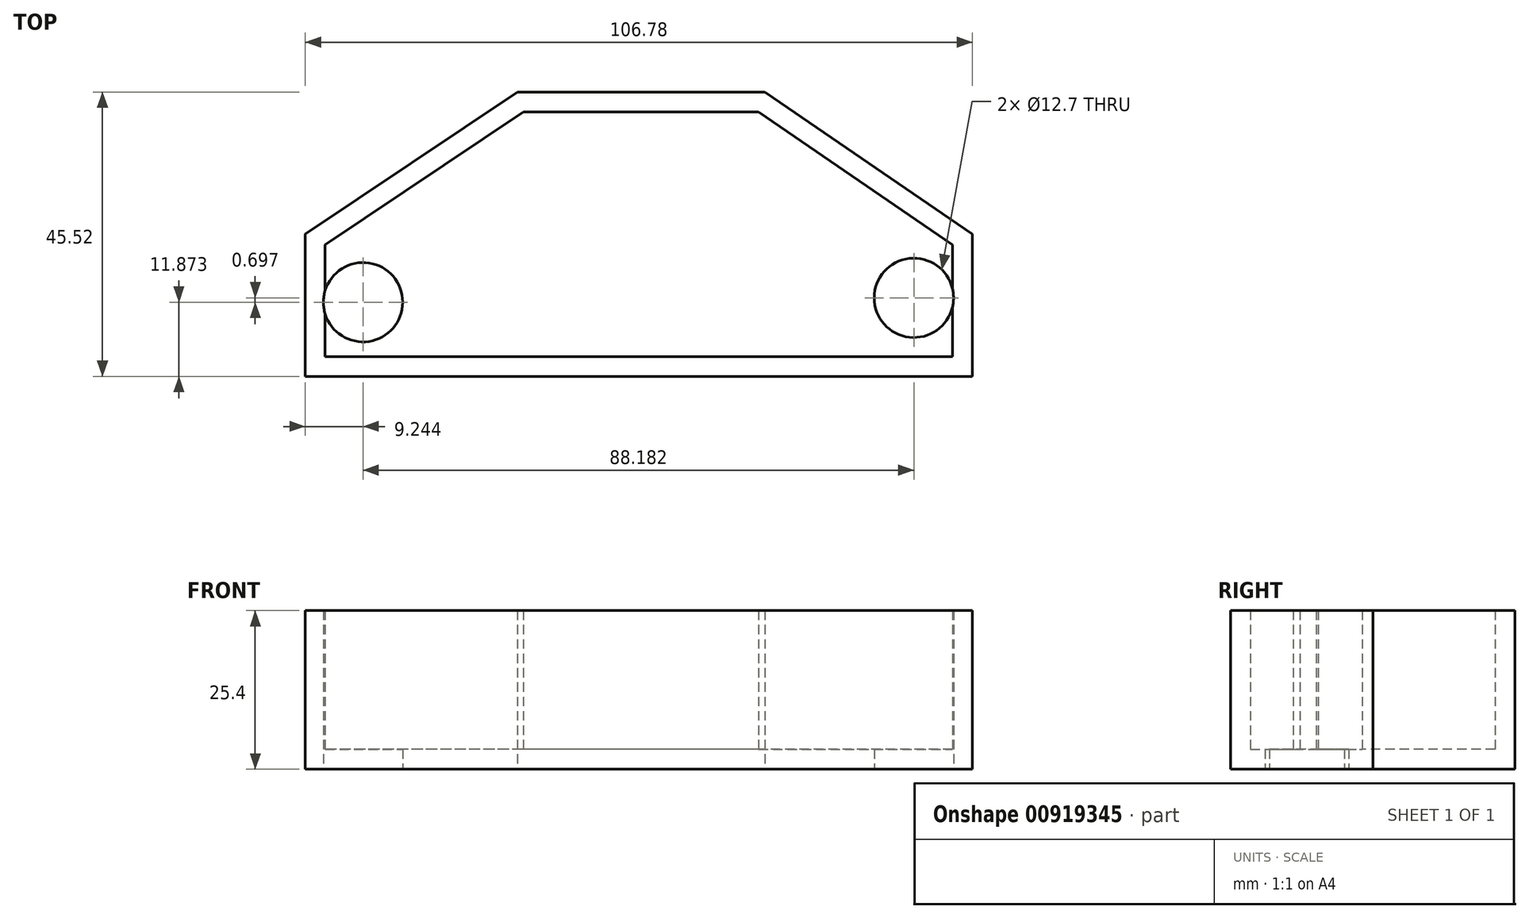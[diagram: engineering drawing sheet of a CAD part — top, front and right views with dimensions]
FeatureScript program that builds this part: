
annotation { "Feature Type Name" : "Feature", "Feature Type Description" : "" }
export const myFeature = defineFeature(function(context is Context, id is Id, definition is map)
    precondition{}
    {
        {
            var Q0;
            Q0=qCreatedBy(makeId("Top.planeOp"),FACE);
            var sketch = newSketch(context, id + "F0", { "sketchPlane" : qUnion([Q0])});
            skLineSegment(sketch, "E0.bottom", {"start": v(53.4, -22.76) * mm, "end": v(-53.4, -22.76) * mm});
            skLineSegment(sketch, "E0.top", {"start": v(20.18, 22.76) * mm, "end": v(-19.45, 22.76) * mm});
            skLineSegment(sketch, "E0.left", {"start": v(53.4, -22.76) * mm, "end": v(53.4, 0) * mm});
            skLineSegment(sketch, "E0.right", {"start": v(-53.4, -22.76) * mm, "end": v(-53.4, 0) * mm});
            skPoint(sketch, "E0.middle", {"position": v(0, 0) * mm});
            skLineSegment(sketch, "E1", {"start": v(20.18, 22.76) * mm, "end": v(53.4, 0) * mm});
            skLineSegment(sketch, "E2", {"start": v(-19.45, 22.76) * mm, "end": v(-53.4, 0) * mm});
            skPoint(sketch, "E3.orphan", {"position": v(53.4, 22.76) * mm});
            skPoint(sketch, "E4.orphan", {"position": v(-53.4, 22.76) * mm});
            skLineSegment(sketch, "E5.0", {"start": v(50.22, -19.59) * mm, "end": v(50.22, -1.67) * mm});
            skLineSegment(sketch, "E5.1", {"start": v(-50.22, -19.59) * mm, "end": v(-50.22, -1.7) * mm});
            skLineSegment(sketch, "E5.2", {"start": v(-18.48, 19.59) * mm, "end": v(-50.22, -1.7) * mm});
            skLineSegment(sketch, "E5.3", {"start": v(50.22, -19.59) * mm, "end": v(-50.22, -19.59) * mm});
            skLineSegment(sketch, "E5.4", {"start": v(19.2, 19.59) * mm, "end": v(-18.48, 19.59) * mm});
            skLineSegment(sketch, "E5.5", {"start": v(19.2, 19.59) * mm, "end": v(50.22, -1.67) * mm});
            skCircle(sketch, "E6", {"center": v(-44.15, -10.89) * mm, "radius": 3.18 * mm});
            skCircle(sketch, "E7", {"center": v(44.04, -10.19) * mm, "radius": 3.18 * mm});
            skCircle(sketch, "E8", {"center": v(44.04, -10.19) * mm, "radius": 6.35 * mm});
            skCircle(sketch, "E9", {"center": v(-44.15, -10.89) * mm, "radius": 6.35 * mm});
            skSolve(sketch);
        }
        {
            var Q0;
            Q0=makeQuery(id+"F0.imprint","IMPRINT",FACE,{"disambiguationData":[TD([[makeQuery(id+"F0.imprint","IMPRINT",EDGE,{"derivedFrom":sQuery(id+"F0.wireOp",EDGE,"E0.bottom")}),-1.0]])]});
            extrude(context, id + "F1", {"entities" : qUnion([Q0]), "depth" : 25.4 * mm, "offsetDistance" : 25.4 * mm});
        }
        {
            var Q0;
            Q0=makeQuery(id+"F0.imprint","IMPRINT",FACE,{"disambiguationData":[TD([[makeQuery(id+"F0.imprint","IMPRINT",EDGE,{"derivedFrom":sQuery(id+"F0.wireOp",EDGE,"E5.0")}),1.0]])]});
            extrude(context, id + "F2", {"entities" : qUnion([Q0]), "operationType" : NewBodyOperationType.ADD, "depth" : 3.17 * mm, "offsetDistance" : 25.4 * mm});
        }
    });
